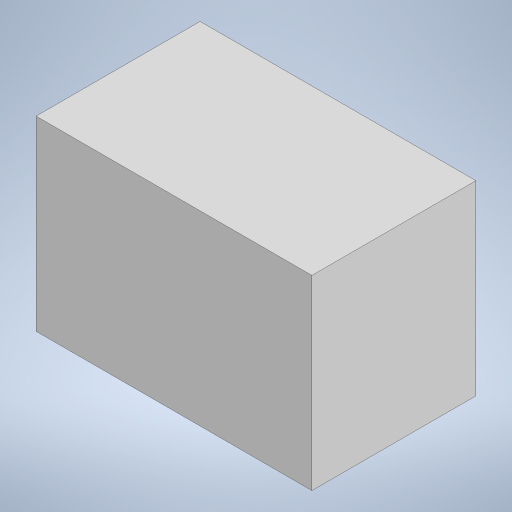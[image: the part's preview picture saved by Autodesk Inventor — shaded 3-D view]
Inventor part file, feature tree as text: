
AUTODESK INVENTOR PART (.ipt)
format: ipt  version: 2024 (Build 280153000, 153)  size: 158,720 bytes
history: native  units: mm
features: other x1, extrude x1, sketch x1
ambient origin geometry x8: Origin, YZ Plane, XZ Plane, XY Plane, X Axis, Y Axis, Z Axis, Center Point
bodies: Body1 (feature_tree)
feature tree (3):
  other  "Bryła1"
  extrude  "Wyciągnięcie proste1"  Depth=18.5mm
  sketch  "Szkic1"
